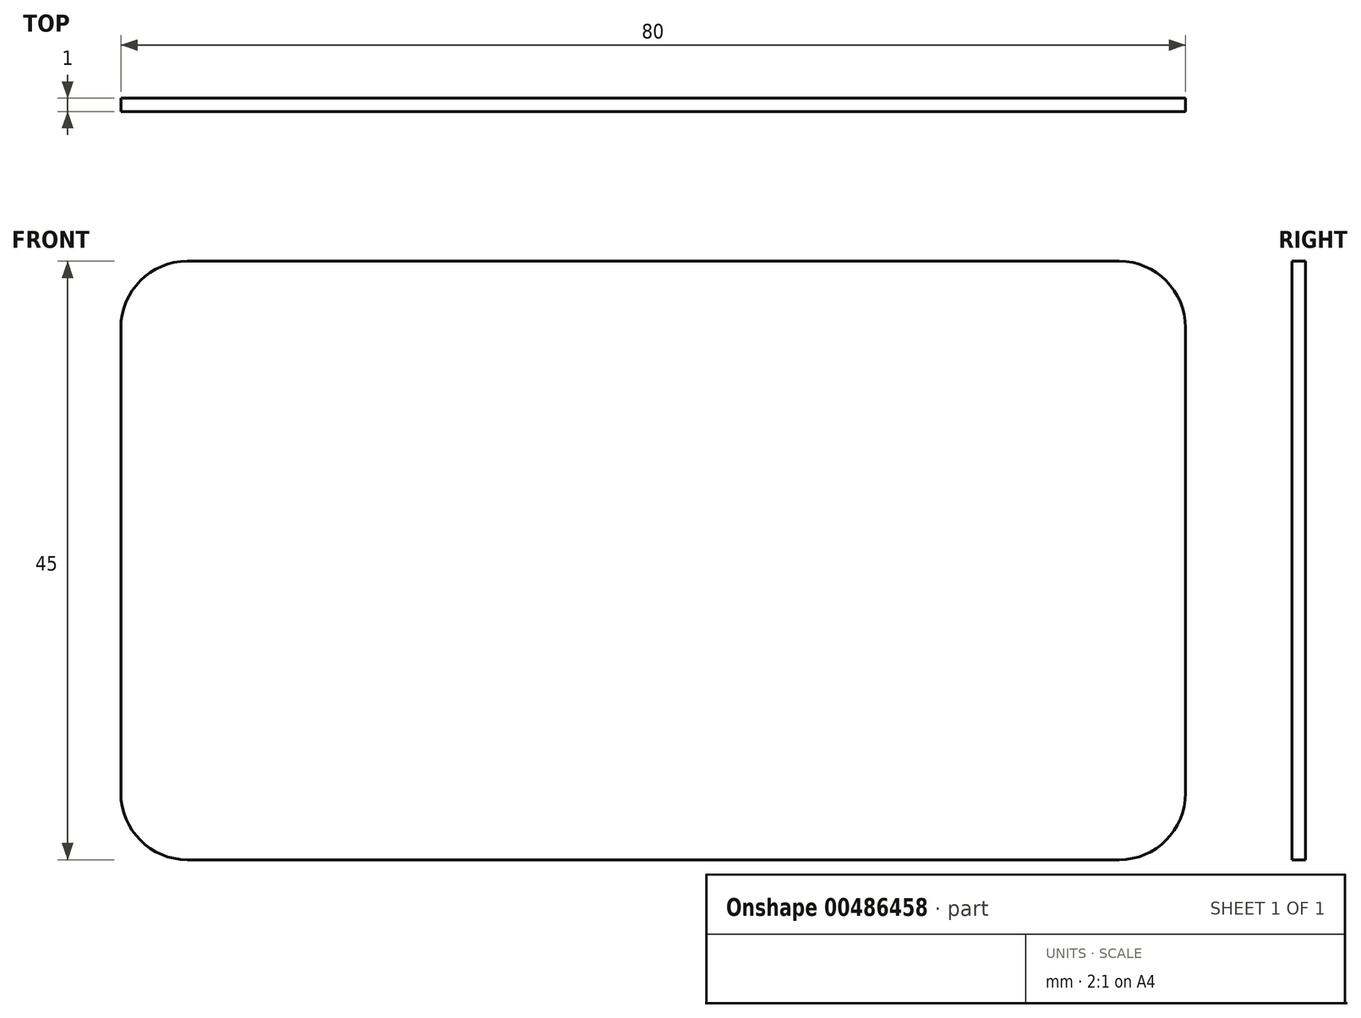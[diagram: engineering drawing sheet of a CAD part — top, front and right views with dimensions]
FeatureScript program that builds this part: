
annotation { "Feature Type Name" : "Feature", "Feature Type Description" : "" }
export const myFeature = defineFeature(function(context is Context, id is Id, definition is map)
    precondition{}
    {
        {
            var Q0;
            Q0=qCreatedBy(makeId("Front.planeOp"),FACE);
            var sketch = newSketch(context, id + "F0", { "sketchPlane" : qUnion([Q0])});
            skLineSegment(sketch, "E0", {"start": v(0, 0) * mm, "end": v(80, 0) * mm});
            skLineSegment(sketch, "E1", {"start": v(0, 0) * mm, "end": v(0, 0) * mm});
            skLineSegment(sketch, "E2", {"start": v(80, 0) * mm, "end": v(80, 0) * mm});
            skLineSegment(sketch, "E3", {"start": v(75, 5) * mm, "end": v(5, 5) * mm});
            skLineSegment(sketch, "E4", {"start": v(80, 0) * mm, "end": v(80, -35) * mm});
            skLineSegment(sketch, "E5", {"start": v(0, 0) * mm, "end": v(0, -35) * mm});
            skLineSegment(sketch, "E6", {"start": v(5, -40) * mm, "end": v(75, -40) * mm});
            skPoint(sketch, "E7.visualSharp", {"position": v(0, 5) * mm});
            skArc(sketch, "E7.filletArc", {"start": v(5, 5) * mm, "mid": v(1.46, 3.54) * mm, "end": v(0, 0) * mm});
            skPoint(sketch, "E8.visualSharp", {"position": v(80, 5) * mm});
            skArc(sketch, "E8.filletArc", {"start": v(80, 0) * mm, "mid": v(78.54, 3.54) * mm, "end": v(75, 5) * mm});
            skPoint(sketch, "E9.visualSharp", {"position": v(80, -40) * mm});
            skArc(sketch, "E9.filletArc", {"start": v(75, -40) * mm, "mid": v(78.54, -38.54) * mm, "end": v(80, -35) * mm});
            skPoint(sketch, "E10.visualSharp", {"position": v(0, -40) * mm});
            skArc(sketch, "E10.filletArc", {"start": v(0, -35) * mm, "mid": v(1.46, -38.54) * mm, "end": v(5, -40) * mm});
            skSolve(sketch);
        }
        {
            var Q0;
            Q0=makeQuery(id+"F0.imprint","IMPRINT",FACE,{"disambiguationData":[TD([[makeQuery(id+"F0.imprint","IMPRINT",EDGE,{"derivedFrom":sQuery(id+"F0.wireOp",EDGE,"E0")}),1.0]])]});
            var Q1;
            Q1=makeQuery(id+"F0.imprint","IMPRINT",FACE,{"disambiguationData":[TD([[makeQuery(id+"F0.imprint","IMPRINT",EDGE,{"derivedFrom":sQuery(id+"F0.wireOp",EDGE,"E0")}),-1.0]])]});
            extrude(context, id + "F1", {"entities" : qUnion([Q0, Q1]), "endBound" : BoundingType.SYMMETRIC, "depth" : 1 * mm, "offsetDistance" : 25 * mm});
        }
    });
